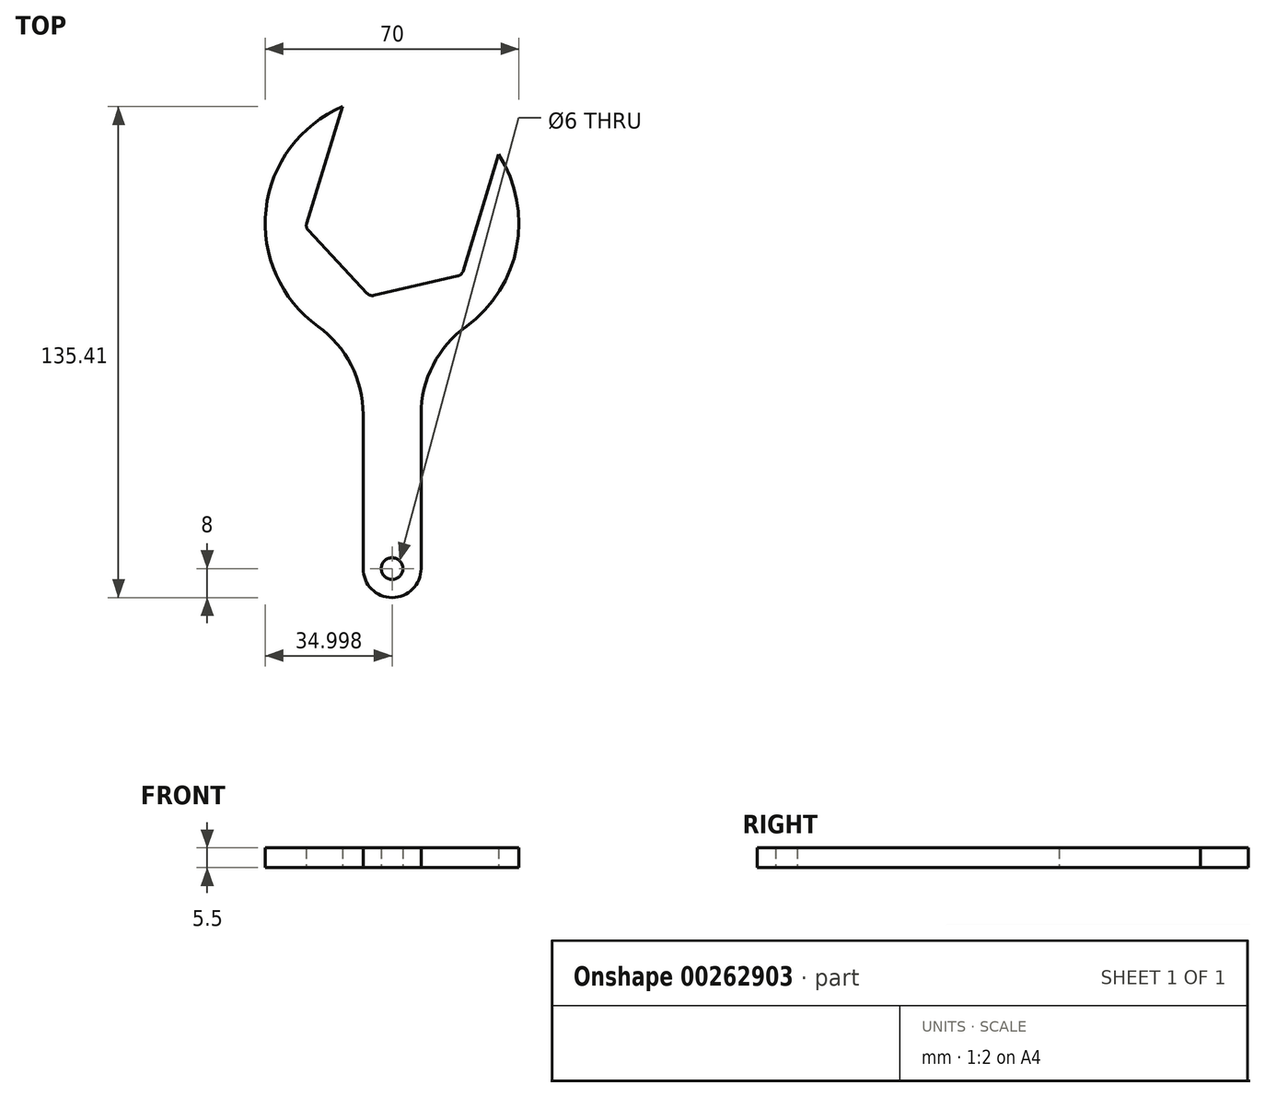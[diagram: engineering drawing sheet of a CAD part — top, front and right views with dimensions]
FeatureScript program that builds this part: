
annotation { "Feature Type Name" : "Feature", "Feature Type Description" : "" }
export const myFeature = defineFeature(function(context is Context, id is Id, definition is map)
    precondition{}
    {
        {
            var Q0;
            Q0=qCreatedBy(makeId("Top.planeOp"),FACE);
            var sketch = newSketch(context, id + "F0", { "sketchPlane" : qUnion([Q0])});
            skCircle(sketch, "E0.cCircle", {"center": v(0, 0) * mm, "radius": 22.55 * mm, "construction": true});
            skLineSegment(sketch, "E0.0", {"start": v(27.93, 14.22) * mm, "end": v(18.1, -17.94) * mm});
            skLineSegment(sketch, "E0.1", {"start": v(16.63, -19.3) * mm, "end": v(-6.49, -24.64) * mm});
            skLineSegment(sketch, "E0.2", {"start": v(-8.4, -24.06) * mm, "end": v(-24.58, -6.7) * mm});
            skLineSegment(sketch, "E0.3", {"start": v(-25.03, -4.75) * mm, "end": v(-15.2, 27.4) * mm});
            skLineSegment(sketch, "E0.4", {"start": v(-17.76, 19.04) * mm, "end": v(7.61, 24.9) * mm, "construction": true});
            skLineSegment(sketch, "E0.5", {"start": v(7.61, 24.9) * mm, "end": v(25.37, 5.86) * mm, "construction": true});
            skPoint(sketch, "E0.0.midPoint", {"position": v(21.56, -6.6) * mm});
            skArc(sketch, "E1", {"start": v(-9.46, -100) * mm, "mid": v(-1.46, -108) * mm, "end": v(6.54, -100) * mm});
            skLineSegment(sketch, "E2.trimOffspring", {"start": v(6.54, -57.52) * mm, "end": v(6.54, -100) * mm});
            skLineSegment(sketch, "E3.trimOffspring", {"start": v(-9.46, -57.52) * mm, "end": v(-9.46, -100) * mm});
            skCircle(sketch, "E4", {"center": v(-1.46, -100) * mm, "radius": 3 * mm});
            skPoint(sketch, "E5.visualSharp", {"position": v(25.37, 5.86) * mm});
            skPoint(sketch, "E6.visualSharp", {"position": v(-17.76, 19.04) * mm});
            skLineSegment(sketch, "E7", {"start": v(-6.6, -21.56) * mm, "end": v(6.6, 21.56) * mm, "construction": true});
            skArc(sketch, "E8", {"start": v(19, -33.18) * mm, "mid": v(32.93, -11.26) * mm, "end": v(27.93, 14.22) * mm});
            skArc(sketch, "E9", {"start": v(-9.46, -38.85) * mm, "mid": v(-1.46, -39.78) * mm, "end": v(6.54, -38.85) * mm, "construction": true});
            skLineSegment(sketch, "E10", {"start": v(-1.46, -4.78) * mm, "end": v(-1.46, -100) * mm, "construction": true});
            skLineSegment(sketch, "E11", {"start": v(-15.2, 27.4) * mm, "end": v(-15.2, 27.4) * mm});
            skArc(sketch, "E12", {"start": v(-15.2, 27.4) * mm, "mid": v(-36.25, -0.92) * mm, "end": v(-21.92, -33.18) * mm});
            skArc(sketch, "E13", {"start": v(27.93, 14.22) * mm, "mid": v(8.77, 28.69) * mm, "end": v(-15.2, 27.4) * mm, "construction": true});
            skPoint(sketch, "E14.visualSharp", {"position": v(6.54, -38.85) * mm});
            skArc(sketch, "E14.filletArc", {"start": v(19, -33.18) * mm, "mid": v(9.83, -43.84) * mm, "end": v(6.54, -57.52) * mm});
            skPoint(sketch, "E15.visualSharp", {"position": v(-9.46, -38.85) * mm});
            skArc(sketch, "E15.filletArc", {"start": v(-9.46, -57.52) * mm, "mid": v(-12.76, -43.84) * mm, "end": v(-21.92, -33.18) * mm});
            skPoint(sketch, "E16.visualSharp", {"position": v(-25.37, -5.86) * mm});
            skArc(sketch, "E16.filletArc", {"start": v(-25.03, -4.75) * mm, "mid": v(-25.07, -5.79) * mm, "end": v(-24.58, -6.7) * mm});
            skPoint(sketch, "E17.visualSharp", {"position": v(-7.61, -24.9) * mm});
            skArc(sketch, "E17.filletArc", {"start": v(-8.4, -24.06) * mm, "mid": v(-7.52, -24.6) * mm, "end": v(-6.49, -24.64) * mm});
            skPoint(sketch, "E18.visualSharp", {"position": v(17.76, -19.04) * mm});
            skArc(sketch, "E18.filletArc", {"start": v(16.63, -19.3) * mm, "mid": v(17.55, -18.82) * mm, "end": v(18.1, -17.94) * mm});
            skSolve(sketch);
        }
        {
            var Q0;
            Q0=qSketchRegion(id+"F0",true);
            extrude(context, id + "F1", {"entities" : qUnion([Q0]), "depth" : 5.5 * mm});
        }
    });
